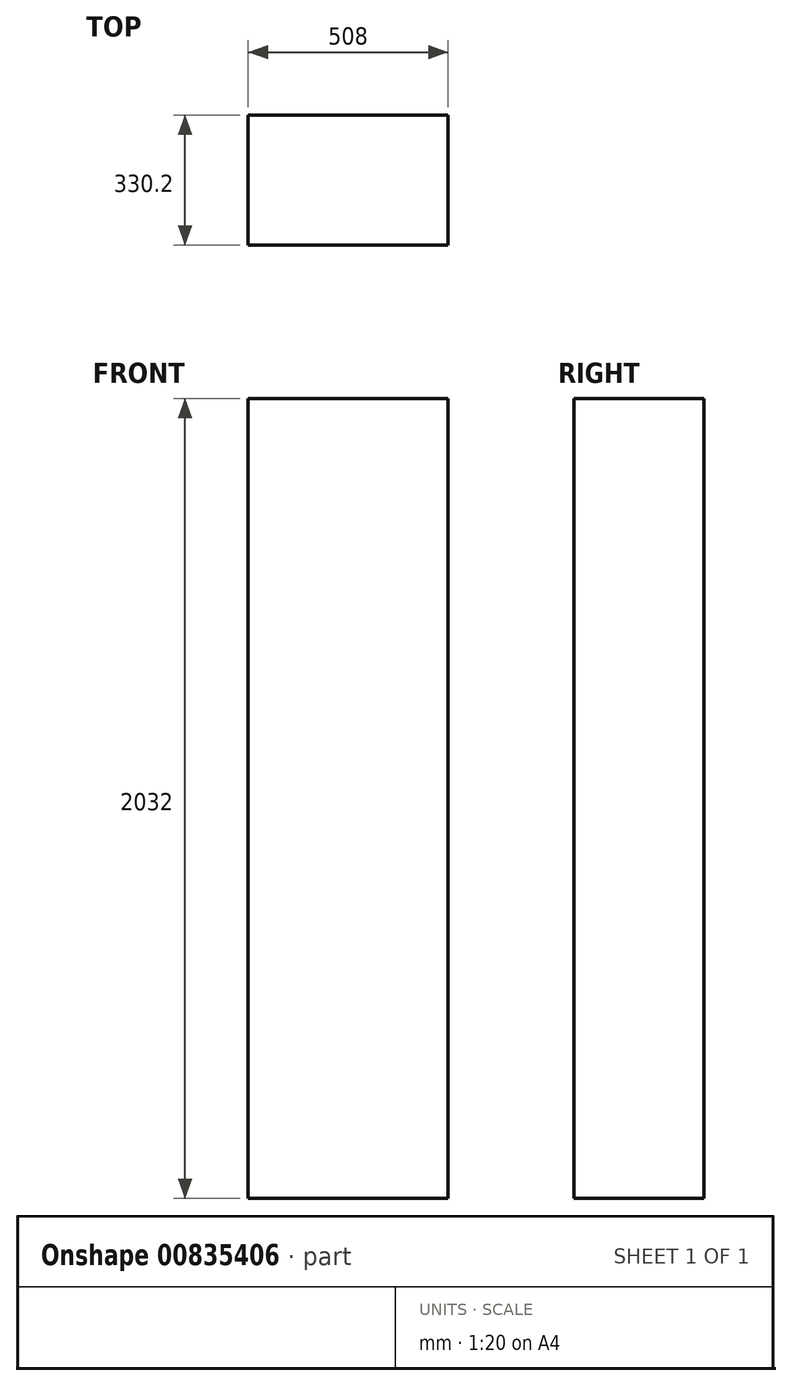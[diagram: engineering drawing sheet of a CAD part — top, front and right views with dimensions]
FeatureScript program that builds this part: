
annotation { "Feature Type Name" : "Feature", "Feature Type Description" : "" }
export const myFeature = defineFeature(function(context is Context, id is Id, definition is map)
    precondition{}
    {
        {
            var Q0;
            Q0=qCreatedBy(makeId("Top.planeOp"),FACE);
            var sketch = newSketch(context, id + "F0", { "sketchPlane" : qUnion([Q0])});
            skLineSegment(sketch, "E0.bottom", {"start": v(-526.7, -289.16) * mm, "end": v(-18.7, -289.16) * mm});
            skLineSegment(sketch, "E0.top", {"start": v(-526.7, 41.04) * mm, "end": v(-18.7, 41.04) * mm});
            skLineSegment(sketch, "E0.left", {"start": v(-526.7, -289.16) * mm, "end": v(-526.7, 41.04) * mm});
            skLineSegment(sketch, "E0.right", {"start": v(-18.7, -289.16) * mm, "end": v(-18.7, 41.04) * mm});
            skSolve(sketch);
        }
        {
            var Q0;
            Q0=makeQuery(id+"F0.imprint","IMPRINT",FACE,{"disambiguationData":[TD([[makeQuery(id+"F0.imprint","IMPRINT",EDGE,{"derivedFrom":sQuery(id+"F0.wireOp",EDGE,"E0.bottom")}),1.0]])]});
            extrude(context, id + "F1", {"entities" : qUnion([Q0]), "depth" : 2032 * mm, "offsetDistance" : 25.4 * mm});
        }
    });
